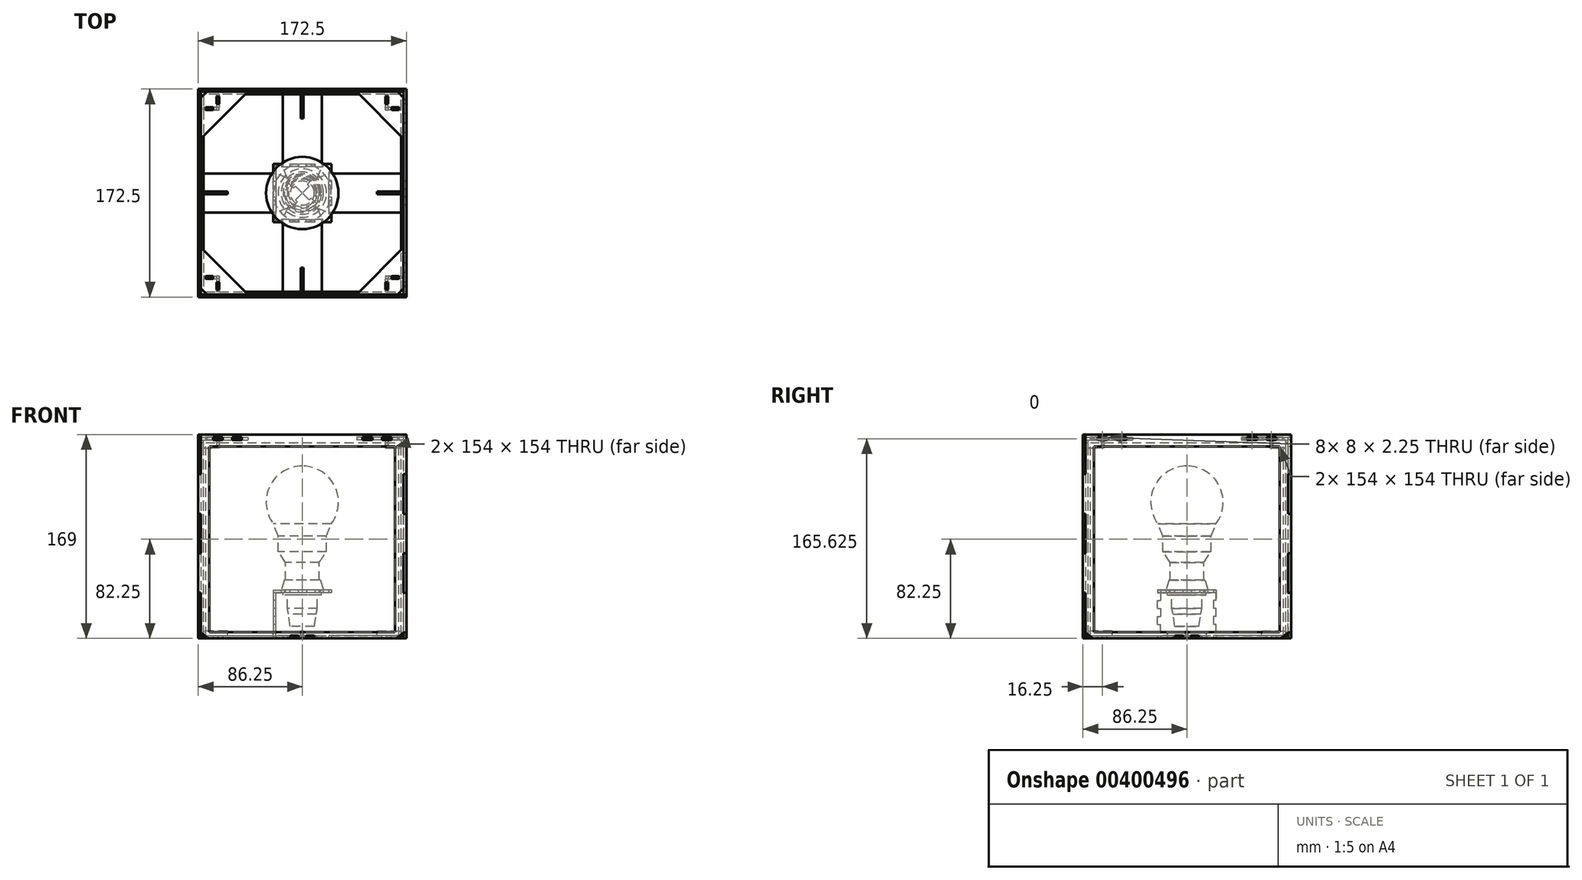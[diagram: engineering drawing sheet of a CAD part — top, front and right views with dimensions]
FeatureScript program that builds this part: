
annotation { "Feature Type Name" : "Feature", "Feature Type Description" : "" }
export const myFeature = defineFeature(function(context is Context, id is Id, definition is map)
    precondition{}
    {
        {
            assignVariable(context, id + "F0", {"name" : "ep", "anyValue" : 2.25});
        }
        {
            var Q0;
            Q0=qCreatedBy(makeId("Front.planeOp"),FACE);
            var sketch = newSketch(context, id + "F1", { "sketchPlane" : qUnion([Q0])});
            skLineSegment(sketch, "E0", {"start": v(0, 10) * mm, "end": v(10, 10) * mm});
            skLineSegment(sketch, "E1", {"start": v(10, 10) * mm, "end": v(11.5, 20) * mm});
            skLineSegment(sketch, "E2", {"start": v(11.5, 20) * mm, "end": v(12.5, 25) * mm});
            skLineSegment(sketch, "E3", {"start": v(12.5, 25) * mm, "end": v(12.5, 36) * mm});
            skLineSegment(sketch, "E4", {"start": v(12.5, 36) * mm, "end": v(16, 36) * mm});
            skLineSegment(sketch, "E5", {"start": v(16, 36) * mm, "end": v(16, 38) * mm});
            skLineSegment(sketch, "E6", {"start": v(16, 38) * mm, "end": v(14, 38) * mm});
            skLineSegment(sketch, "E7", {"start": v(14, 38) * mm, "end": v(14, 40.25) * mm});
            skLineSegment(sketch, "E8", {"start": v(14, 40.25) * mm, "end": v(17.5, 40.25) * mm});
            skLineSegment(sketch, "E9", {"start": v(17.5, 40.25) * mm, "end": v(15, 48.25) * mm});
            skLineSegment(sketch, "E10", {"start": v(15, 48.25) * mm, "end": v(14, 48.25) * mm});
            skLineSegment(sketch, "E11", {"start": v(14, 48.25) * mm, "end": v(14, 63) * mm});
            skLineSegment(sketch, "E12", {"start": v(14, 63) * mm, "end": v(20, 72) * mm});
            skLineSegment(sketch, "E13", {"start": v(20, 72) * mm, "end": v(20, 85) * mm});
            skLineSegment(sketch, "E14", {"start": v(20, 85) * mm, "end": v(24, 95) * mm});
            skLineSegment(sketch, "E15", {"start": v(0, 10) * mm, "end": v(0, 113) * mm, "construction": true});
            skArc(sketch, "E16", {"start": v(24, 95) * mm, "mid": v(26.83, 126.42) * mm, "end": v(0, 143) * mm});
            skLineSegment(sketch, "E17", {"start": v(0, 143) * mm, "end": v(0, 10) * mm});
            skSolve(sketch);
        }
        {
            var Q0;
            Q0=qSketchRegion(id+"F1",true);
            var Q1;
            Q1=sQuery(id+"F1.wireOp",EDGE,"E17");
            revolve(context, id + "F2", {"entities" : qUnion([Q0]), "axis" : qUnion([Q1]), "revolveType" : RevolveType.FULL});
        }
        {
            var Q0;
            Q0=makeQuery(id+"F2.opRevolve","SWEPT_FACE",FACE,{"disambiguationData":[OSD([sQuery(id+"F1.wireOp",EDGE,"E6")])]});
            var sketch = newSketch(context, id + "F3", { "sketchPlane" : qUnion([Q0])});
            skCircle(sketch, "E18.0", {"center": v(0, 0) * mm, "radius": 15 * mm});
            skLineSegment(sketch, "E19.top", {"start": v(-17.32, 22) * mm, "end": v(-10.4, 22) * mm});
            skLineSegment(sketch, "E19.left", {"start": v(-17.32, 24.25) * mm, "end": v(-17.32, 22) * mm});
            skLineSegment(sketch, "E19.right", {"start": v(-10.4, 24.25) * mm, "end": v(-10.4, 22) * mm});
            skLineSegment(sketch, "E20.1.0.0", {"start": v(3.46, 24.25) * mm, "end": v(3.46, 22) * mm});
            skLineSegment(sketch, "E20.1.0.1", {"start": v(-3.46, 22) * mm, "end": v(3.46, 22) * mm});
            skLineSegment(sketch, "E20.1.0.3", {"start": v(-3.46, 24.25) * mm, "end": v(-3.46, 22) * mm});
            skLineSegment(sketch, "E20.2.0.0", {"start": v(17.32, 24.25) * mm, "end": v(17.32, 22) * mm});
            skLineSegment(sketch, "E20.2.0.1", {"start": v(10.4, 22) * mm, "end": v(17.32, 22) * mm});
            skLineSegment(sketch, "E20.2.0.3", {"start": v(10.4, 24.25) * mm, "end": v(10.4, 22) * mm});
            skLineSegment(sketch, "E21", {"start": v(-24.25, 24.25) * mm, "end": v(-17.32, 24.25) * mm});
            skLineSegment(sketch, "E22", {"start": v(-10.4, 24.25) * mm, "end": v(-3.46, 24.25) * mm});
            skLineSegment(sketch, "E23", {"start": v(3.46, 24.25) * mm, "end": v(10.4, 24.25) * mm});
            skLineSegment(sketch, "E24", {"start": v(17.32, 24.25) * mm, "end": v(24.25, 24.25) * mm});
            skLineSegment(sketch, "E25.1.0", {"start": v(-24.25, -3.46) * mm, "end": v(-22, -3.46) * mm});
            skLineSegment(sketch, "E25.1.1", {"start": v(-22, -3.46) * mm, "end": v(-22, 3.46) * mm});
            skLineSegment(sketch, "E25.1.2", {"start": v(-24.25, 17.32) * mm, "end": v(-22, 17.32) * mm});
            skLineSegment(sketch, "E25.1.3", {"start": v(-24.25, 3.46) * mm, "end": v(-24.25, 10.4) * mm});
            skLineSegment(sketch, "E25.1.4", {"start": v(-24.25, 3.46) * mm, "end": v(-22, 3.46) * mm});
            skLineSegment(sketch, "E25.1.5", {"start": v(-24.25, -10.4) * mm, "end": v(-24.25, -3.46) * mm});
            skLineSegment(sketch, "E25.1.6", {"start": v(-24.25, -10.4) * mm, "end": v(-22, -10.4) * mm});
            skLineSegment(sketch, "E25.1.7", {"start": v(-24.25, -24.25) * mm, "end": v(-24.25, -17.32) * mm});
            skLineSegment(sketch, "E25.1.8", {"start": v(-24.25, 10.4) * mm, "end": v(-22, 10.4) * mm});
            skLineSegment(sketch, "E25.1.9", {"start": v(-24.25, -17.32) * mm, "end": v(-22, -17.32) * mm});
            skLineSegment(sketch, "E25.1.10", {"start": v(-22, 10.4) * mm, "end": v(-22, 17.32) * mm});
            skLineSegment(sketch, "E25.1.11", {"start": v(-24.25, 17.32) * mm, "end": v(-24.25, 24.25) * mm});
            skLineSegment(sketch, "E25.1.12", {"start": v(-22, -17.32) * mm, "end": v(-22, -10.4) * mm});
            skLineSegment(sketch, "E25.2.0", {"start": v(3.46, -24.25) * mm, "end": v(3.46, -22) * mm});
            skLineSegment(sketch, "E25.2.1", {"start": v(3.46, -22) * mm, "end": v(-3.46, -22) * mm});
            skLineSegment(sketch, "E25.2.2", {"start": v(-17.32, -24.25) * mm, "end": v(-17.32, -22) * mm});
            skLineSegment(sketch, "E25.2.3", {"start": v(-3.46, -24.25) * mm, "end": v(-10.4, -24.25) * mm});
            skLineSegment(sketch, "E25.2.4", {"start": v(-3.46, -24.25) * mm, "end": v(-3.46, -22) * mm});
            skLineSegment(sketch, "E25.2.5", {"start": v(10.4, -24.25) * mm, "end": v(3.46, -24.25) * mm});
            skLineSegment(sketch, "E25.2.6", {"start": v(10.4, -24.25) * mm, "end": v(10.4, -22) * mm});
            skLineSegment(sketch, "E25.2.7", {"start": v(24.25, -24.25) * mm, "end": v(17.32, -24.25) * mm});
            skLineSegment(sketch, "E25.2.8", {"start": v(-10.4, -24.25) * mm, "end": v(-10.4, -22) * mm});
            skLineSegment(sketch, "E25.2.9", {"start": v(17.32, -24.25) * mm, "end": v(17.32, -22) * mm});
            skLineSegment(sketch, "E25.2.10", {"start": v(-10.4, -22) * mm, "end": v(-17.32, -22) * mm});
            skLineSegment(sketch, "E25.2.11", {"start": v(-17.32, -24.25) * mm, "end": v(-24.25, -24.25) * mm});
            skLineSegment(sketch, "E25.2.12", {"start": v(17.32, -22) * mm, "end": v(10.4, -22) * mm});
            skLineSegment(sketch, "E25.3.0", {"start": v(24.25, 3.46) * mm, "end": v(22, 3.46) * mm});
            skLineSegment(sketch, "E25.3.1", {"start": v(22, 3.46) * mm, "end": v(22, -3.46) * mm});
            skLineSegment(sketch, "E25.3.2", {"start": v(24.25, -17.32) * mm, "end": v(22, -17.32) * mm});
            skLineSegment(sketch, "E25.3.3", {"start": v(24.25, -3.46) * mm, "end": v(24.25, -10.4) * mm});
            skLineSegment(sketch, "E25.3.4", {"start": v(24.25, -3.46) * mm, "end": v(22, -3.46) * mm});
            skLineSegment(sketch, "E25.3.5", {"start": v(24.25, 10.4) * mm, "end": v(24.25, 3.46) * mm});
            skLineSegment(sketch, "E25.3.6", {"start": v(24.25, 10.4) * mm, "end": v(22, 10.4) * mm});
            skLineSegment(sketch, "E25.3.7", {"start": v(24.25, 24.25) * mm, "end": v(24.25, 17.32) * mm});
            skLineSegment(sketch, "E25.3.8", {"start": v(24.25, -10.4) * mm, "end": v(22, -10.4) * mm});
            skLineSegment(sketch, "E25.3.9", {"start": v(24.25, 17.32) * mm, "end": v(22, 17.32) * mm});
            skLineSegment(sketch, "E25.3.10", {"start": v(22, -10.4) * mm, "end": v(22, -17.32) * mm});
            skLineSegment(sketch, "E25.3.11", {"start": v(24.25, -17.32) * mm, "end": v(24.25, -24.25) * mm});
            skLineSegment(sketch, "E25.3.12", {"start": v(22, 17.32) * mm, "end": v(22, 10.4) * mm});
            skSolve(sketch);
        }
        {
            var Q0;
            Q0=makeQuery(id+"F3.imprint","IMPRINT",FACE,{"disambiguationData":[TD([[makeQuery(id+"F3.imprint","IMPRINT",EDGE,{"derivedFrom":sQuery(id+"F3.wireOp",EDGE,"E19.top")}),-1.0]])]});
            var Q1;
            Q1=makeQuery(id+"F3.imprint","IMPRINT",FACE,{"disambiguationData":[TD([[makeQuery(id+"F3.imprint","IMPRINT",EDGE,{"derivedFrom":sQuery(id+"F3.wireOp",EDGE,"E18.0")}),-1.0]])]});
            extrude(context, id + "F4", {"entities" : qUnion([Q0, Q1]), "depth" : (getVariable(context, 'ep')) * mm});
        }
        {
            var Q0;
            Q0=makeQuery(id+"F4.opExtrude","CAP_FACE",FACE,{"disambiguationData":[OSD([sQuery(id+"F3.wireOp",EDGE,"E18.0"),sQuery(id+"F3.wireOp",EDGE,"E19.top"),sQuery(id+"F3.wireOp",EDGE,"E19.left"),sQuery(id+"F3.wireOp",EDGE,"E19.right"),sQuery(id+"F3.wireOp",EDGE,"E20.1.0.0"),sQuery(id+"F3.wireOp",EDGE,"E20.1.0.1"),sQuery(id+"F3.wireOp",EDGE,"E20.1.0.3"),sQuery(id+"F3.wireOp",EDGE,"E20.2.0.0"),sQuery(id+"F3.wireOp",EDGE,"E20.2.0.1"),sQuery(id+"F3.wireOp",EDGE,"E20.2.0.3"),sQuery(id+"F3.wireOp",EDGE,"E21"),sQuery(id+"F3.wireOp",EDGE,"E22"),sQuery(id+"F3.wireOp",EDGE,"E23"),sQuery(id+"F3.wireOp",EDGE,"E24"),sQuery(id+"F3.wireOp",EDGE,"E25.1.0"),sQuery(id+"F3.wireOp",EDGE,"E25.1.1"),sQuery(id+"F3.wireOp",EDGE,"E25.1.2"),sQuery(id+"F3.wireOp",EDGE,"E25.1.3"),sQuery(id+"F3.wireOp",EDGE,"E25.1.4"),sQuery(id+"F3.wireOp",EDGE,"E25.1.5"),sQuery(id+"F3.wireOp",EDGE,"E25.1.6"),sQuery(id+"F3.wireOp",EDGE,"E25.1.7"),sQuery(id+"F3.wireOp",EDGE,"E25.1.8"),sQuery(id+"F3.wireOp",EDGE,"E25.1.9"),sQuery(id+"F3.wireOp",EDGE,"E25.1.10"),sQuery(id+"F3.wireOp",EDGE,"E25.1.11"),sQuery(id+"F3.wireOp",EDGE,"E25.1.12"),sQuery(id+"F3.wireOp",EDGE,"E25.2.0"),sQuery(id+"F3.wireOp",EDGE,"E25.2.1"),sQuery(id+"F3.wireOp",EDGE,"E25.2.2"),sQuery(id+"F3.wireOp",EDGE,"E25.2.3"),sQuery(id+"F3.wireOp",EDGE,"E25.2.4"),sQuery(id+"F3.wireOp",EDGE,"E25.2.5"),sQuery(id+"F3.wireOp",EDGE,"E25.2.6"),sQuery(id+"F3.wireOp",EDGE,"E25.2.7"),sQuery(id+"F3.wireOp",EDGE,"E25.2.8"),sQuery(id+"F3.wireOp",EDGE,"E25.2.9"),sQuery(id+"F3.wireOp",EDGE,"E25.2.10"),sQuery(id+"F3.wireOp",EDGE,"E25.2.11"),sQuery(id+"F3.wireOp",EDGE,"E25.2.12"),sQuery(id+"F3.wireOp",EDGE,"E25.3.0"),sQuery(id+"F3.wireOp",EDGE,"E25.3.1"),sQuery(id+"F3.wireOp",EDGE,"E25.3.2"),sQuery(id+"F3.wireOp",EDGE,"E25.3.3"),sQuery(id+"F3.wireOp",EDGE,"E25.3.4"),sQuery(id+"F3.wireOp",EDGE,"E25.3.5"),sQuery(id+"F3.wireOp",EDGE,"E25.3.6"),sQuery(id+"F3.wireOp",EDGE,"E25.3.7"),sQuery(id+"F3.wireOp",EDGE,"E25.3.8"),sQuery(id+"F3.wireOp",EDGE,"E25.3.9"),sQuery(id+"F3.wireOp",EDGE,"E25.3.10"),sQuery(id+"F3.wireOp",EDGE,"E25.3.11"),sQuery(id+"F3.wireOp",EDGE,"E25.3.12")])],"isStart":true});
            var sketch = newSketch(context, id + "F5", { "sketchPlane" : qUnion([Q0])});
            skLineSegment(sketch, "E26.left", {"start": v(-24.25, 24.25) * mm, "end": v(-24.25, -24.25) * mm});
            skLineSegment(sketch, "E26.right", {"start": v(24.25, 24.25) * mm, "end": v(24.25, -24.25) * mm});
            skLineSegment(sketch, "E27", {"start": v(22, 24.25) * mm, "end": v(22, -24.25) * mm});
            skLineSegment(sketch, "E28", {"start": v(22, -24.25) * mm, "end": v(24.25, -24.25) * mm});
            skLineSegment(sketch, "E29", {"start": v(22, 24.25) * mm, "end": v(24.25, 24.25) * mm});
            skLineSegment(sketch, "E30", {"start": v(-22, 24.25) * mm, "end": v(-22, -24.25) * mm});
            skLineSegment(sketch, "E31", {"start": v(-22, -24.25) * mm, "end": v(-24.25, -24.25) * mm});
            skLineSegment(sketch, "E32", {"start": v(-24.25, 24.25) * mm, "end": v(-22, 24.25) * mm});
            skSolve(sketch);
        }
        {
            var Q0;
            {var subQ0=sQuery(id+"F5.wireOp",EDGE,"E32");Q0=makeQuery(id+"F5.imprint","IMPRINT",FACE,{"disambiguationData":[TD([[makeQuery(id+"F5.imprint","IMPRINT",EDGE,{"derivedFrom":subQ0}),1.0]])]});}
            var Q1;
            {var subQ1=makeQuery(id+"F4.opExtrude","CAP_EDGE",EDGE,{"disambiguationData":[OSD([sQuery(id+"F3.wireOp",EDGE,"E25.1.6")])],"isStart":true});Q1=makeQuery(id+"F5.imprint","IMPRINT",FACE,{"disambiguationData":[TD([[makeQuery(id+"F5.imprint","IMPRINT",EDGE,{"derivedFrom":subQ1}),1.0]])]});}
            var Q2;
            {var subQ1=makeQuery(id+"F4.opExtrude","CAP_EDGE",EDGE,{"disambiguationData":[OSD([sQuery(id+"F3.wireOp",EDGE,"E25.1.0")])],"isStart":true});Q2=makeQuery(id+"F5.imprint","IMPRINT",FACE,{"disambiguationData":[TD([[makeQuery(id+"F5.imprint","IMPRINT",EDGE,{"derivedFrom":subQ1}),1.0]])]});}
            var Q3;
            {var subQ1=makeQuery(id+"F4.opExtrude","CAP_EDGE",EDGE,{"disambiguationData":[OSD([sQuery(id+"F3.wireOp",EDGE,"E25.1.0")])],"isStart":true});Q3=makeQuery(id+"F5.imprint","IMPRINT",FACE,{"disambiguationData":[TD([[makeQuery(id+"F5.imprint","IMPRINT",EDGE,{"derivedFrom":subQ1}),-1.0]])]});}
            var Q4;
            {var subQ1=makeQuery(id+"F4.opExtrude","CAP_EDGE",EDGE,{"disambiguationData":[OSD([sQuery(id+"F3.wireOp",EDGE,"E25.1.4")])],"isStart":true});Q4=makeQuery(id+"F5.imprint","IMPRINT",FACE,{"disambiguationData":[TD([[makeQuery(id+"F5.imprint","IMPRINT",EDGE,{"derivedFrom":subQ1}),-1.0]])]});}
            var Q5;
            {var subQ1=makeQuery(id+"F4.opExtrude","CAP_EDGE",EDGE,{"disambiguationData":[OSD([sQuery(id+"F3.wireOp",EDGE,"E25.1.2")])],"isStart":true});Q5=makeQuery(id+"F5.imprint","IMPRINT",FACE,{"disambiguationData":[TD([[makeQuery(id+"F5.imprint","IMPRINT",EDGE,{"derivedFrom":subQ1}),1.0]])]});}
            var Q6;
            {var subQ0=sQuery(id+"F5.wireOp",EDGE,"E31");Q6=makeQuery(id+"F5.imprint","IMPRINT",FACE,{"disambiguationData":[TD([[makeQuery(id+"F5.imprint","IMPRINT",EDGE,{"derivedFrom":subQ0}),1.0]])]});}
            var Q7;
            Q7=qCreatedBy(makeId("Top.planeOp"),FACE);
            extrude(context, id + "F6", {"entities" : qUnion([Q0, Q1, Q2, Q3, Q4, Q5, Q6]), "endBound" : BoundingType.UP_TO_SURFACE, "endBoundEntityFace" : qUnion([Q7]), "depth" : 25 * mm});
        }
        {
            var Q0;
            {var subQ1=makeQuery(id+"F4.opExtrude","CAP_EDGE",EDGE,{"disambiguationData":[OSD([sQuery(id+"F3.wireOp",EDGE,"E25.1.2")])],"isStart":true});Q0=makeQuery(id+"F5.imprint","IMPRINT",FACE,{"disambiguationData":[TD([[makeQuery(id+"F5.imprint","IMPRINT",EDGE,{"derivedFrom":subQ1}),1.0]])]});}
            var Q1;
            {var subQ1=makeQuery(id+"F4.opExtrude","CAP_EDGE",EDGE,{"disambiguationData":[OSD([sQuery(id+"F3.wireOp",EDGE,"E25.1.0")])],"isStart":true});Q1=makeQuery(id+"F5.imprint","IMPRINT",FACE,{"disambiguationData":[TD([[makeQuery(id+"F5.imprint","IMPRINT",EDGE,{"derivedFrom":subQ1}),-1.0]])]});}
            var Q2;
            {var subQ1=makeQuery(id+"F4.opExtrude","CAP_EDGE",EDGE,{"disambiguationData":[OSD([sQuery(id+"F3.wireOp",EDGE,"E25.1.6")])],"isStart":true});Q2=makeQuery(id+"F5.imprint","IMPRINT",FACE,{"disambiguationData":[TD([[makeQuery(id+"F5.imprint","IMPRINT",EDGE,{"derivedFrom":subQ1}),1.0]])]});}
            var Q3;
            Q3=makeQuery(id+"F4.opExtrude","CAP_FACE",FACE,{"disambiguationData":[OSD([sQuery(id+"F3.wireOp",EDGE,"E18.0"),sQuery(id+"F3.wireOp",EDGE,"E19.top"),sQuery(id+"F3.wireOp",EDGE,"E19.left"),sQuery(id+"F3.wireOp",EDGE,"E19.right"),sQuery(id+"F3.wireOp",EDGE,"E20.1.0.0"),sQuery(id+"F3.wireOp",EDGE,"E20.1.0.1"),sQuery(id+"F3.wireOp",EDGE,"E20.1.0.3"),sQuery(id+"F3.wireOp",EDGE,"E20.2.0.0"),sQuery(id+"F3.wireOp",EDGE,"E20.2.0.1"),sQuery(id+"F3.wireOp",EDGE,"E20.2.0.3"),sQuery(id+"F3.wireOp",EDGE,"E21"),sQuery(id+"F3.wireOp",EDGE,"E22"),sQuery(id+"F3.wireOp",EDGE,"E23"),sQuery(id+"F3.wireOp",EDGE,"E24"),sQuery(id+"F3.wireOp",EDGE,"E25.1.0"),sQuery(id+"F3.wireOp",EDGE,"E25.1.1"),sQuery(id+"F3.wireOp",EDGE,"E25.1.2"),sQuery(id+"F3.wireOp",EDGE,"E25.1.3"),sQuery(id+"F3.wireOp",EDGE,"E25.1.4"),sQuery(id+"F3.wireOp",EDGE,"E25.1.5"),sQuery(id+"F3.wireOp",EDGE,"E25.1.6"),sQuery(id+"F3.wireOp",EDGE,"E25.1.7"),sQuery(id+"F3.wireOp",EDGE,"E25.1.8"),sQuery(id+"F3.wireOp",EDGE,"E25.1.9"),sQuery(id+"F3.wireOp",EDGE,"E25.1.10"),sQuery(id+"F3.wireOp",EDGE,"E25.1.11"),sQuery(id+"F3.wireOp",EDGE,"E25.1.12"),sQuery(id+"F3.wireOp",EDGE,"E25.2.0"),sQuery(id+"F3.wireOp",EDGE,"E25.2.1"),sQuery(id+"F3.wireOp",EDGE,"E25.2.2"),sQuery(id+"F3.wireOp",EDGE,"E25.2.3"),sQuery(id+"F3.wireOp",EDGE,"E25.2.4"),sQuery(id+"F3.wireOp",EDGE,"E25.2.5"),sQuery(id+"F3.wireOp",EDGE,"E25.2.6"),sQuery(id+"F3.wireOp",EDGE,"E25.2.7"),sQuery(id+"F3.wireOp",EDGE,"E25.2.8"),sQuery(id+"F3.wireOp",EDGE,"E25.2.9"),sQuery(id+"F3.wireOp",EDGE,"E25.2.10"),sQuery(id+"F3.wireOp",EDGE,"E25.2.11"),sQuery(id+"F3.wireOp",EDGE,"E25.2.12"),sQuery(id+"F3.wireOp",EDGE,"E25.3.0"),sQuery(id+"F3.wireOp",EDGE,"E25.3.1"),sQuery(id+"F3.wireOp",EDGE,"E25.3.2"),sQuery(id+"F3.wireOp",EDGE,"E25.3.3"),sQuery(id+"F3.wireOp",EDGE,"E25.3.4"),sQuery(id+"F3.wireOp",EDGE,"E25.3.5"),sQuery(id+"F3.wireOp",EDGE,"E25.3.6"),sQuery(id+"F3.wireOp",EDGE,"E25.3.7"),sQuery(id+"F3.wireOp",EDGE,"E25.3.8"),sQuery(id+"F3.wireOp",EDGE,"E25.3.9"),sQuery(id+"F3.wireOp",EDGE,"E25.3.10"),sQuery(id+"F3.wireOp",EDGE,"E25.3.11"),sQuery(id+"F3.wireOp",EDGE,"E25.3.12")])],"isStart":false});
            extrude(context, id + "F7", {"entities" : qUnion([Q0, Q1, Q2]), "operationType" : NewBodyOperationType.ADD, "endBound" : BoundingType.UP_TO_SURFACE, "oppositeDirection" : true, "endBoundEntityFace" : qUnion([Q3]), "depth" : 25 * mm});
        }
        {
            var Q0;
            {var subQ0=sQuery(id+"F5.wireOp",EDGE,"E26.left");Q0=makeQuery(id+"F7.boolean.opBoolean","MERGE",FACE,{"derivedFrom":[makeQuery(id+"F6.opExtrude","SWEPT_FACE",FACE,{"disambiguationData":[OSD([subQ0])]}),makeQuery(id+"F7.opExtrude","SWEPT_FACE",FACE,{"disambiguationData":[OSD([subQ0]),TDD([makeQuery(id+"F5.imprint","IMPRINT",EDGE,{"disambiguationData":[TD([[makeQuery(id+"F5.imprint","INTERSECT",VERTEX,{"derivedFrom":[makeQuery(id+"F4.opExtrude","CAP_EDGE",EDGE,{"disambiguationData":[OSD([sQuery(id+"F3.wireOp",EDGE,"E25.1.6")])],"isStart":true}),subQ0]}),1.0]])],"derivedFrom":subQ0})])]}),makeQuery(id+"F7.opExtrude","SWEPT_FACE",FACE,{"disambiguationData":[OSD([subQ0]),TDD([makeQuery(id+"F5.imprint","IMPRINT",EDGE,{"disambiguationData":[TD([[makeQuery(id+"F5.imprint","INTERSECT",VERTEX,{"derivedFrom":[makeQuery(id+"F4.opExtrude","CAP_EDGE",EDGE,{"disambiguationData":[OSD([sQuery(id+"F3.wireOp",EDGE,"E25.1.0")])],"isStart":true}),subQ0]}),-1.0]])],"derivedFrom":subQ0})])]}),makeQuery(id+"F7.opExtrude","SWEPT_FACE",FACE,{"disambiguationData":[OSD([subQ0]),TDD([makeQuery(id+"F5.imprint","IMPRINT",EDGE,{"disambiguationData":[TD([[makeQuery(id+"F5.imprint","INTERSECT",VERTEX,{"derivedFrom":[makeQuery(id+"F4.opExtrude","CAP_EDGE",EDGE,{"disambiguationData":[OSD([sQuery(id+"F3.wireOp",EDGE,"E25.1.2")])],"isStart":true}),subQ0]}),1.0]])],"derivedFrom":subQ0})])]})]});}
            var sketch = newSketch(context, id + "F8", { "sketchPlane" : qUnion([Q0])});
            skLineSegment(sketch, "E33.bottom", {"start": v(-24.25, 0) * mm, "end": v(-9.75, 0) * mm});
            skLineSegment(sketch, "E33.top", {"start": v(-24.25, 5) * mm, "end": v(-16.25, 5) * mm});
            skLineSegment(sketch, "E33.left", {"start": v(-24.25, 0) * mm, "end": v(-24.25, 5) * mm});
            skLineSegment(sketch, "E33.right", {"start": v(-16.25, 2.25) * mm, "end": v(-16.25, 5) * mm});
            skLineSegment(sketch, "E34.bottom", {"start": v(24.25, 0) * mm, "end": v(9.75, 0) * mm});
            skLineSegment(sketch, "E34.top", {"start": v(22, 5) * mm, "end": v(16.25, 5) * mm});
            skLineSegment(sketch, "E34.left", {"start": v(24.25, 0) * mm, "end": v(24.25, 5) * mm});
            skLineSegment(sketch, "E34.right", {"start": v(16.25, 2.25) * mm, "end": v(16.25, 5) * mm});
            skLineSegment(sketch, "E35.bottom", {"start": v(-24.25, 31.4) * mm, "end": v(-22, 31.4) * mm});
            skLineSegment(sketch, "E35.top", {"start": v(-24.25, 24.8) * mm, "end": v(-22, 24.8) * mm});
            skLineSegment(sketch, "E35.left", {"start": v(-24.25, 31.4) * mm, "end": v(-24.25, 24.8) * mm});
            skLineSegment(sketch, "E35.right", {"start": v(-22, 31.4) * mm, "end": v(-22, 24.8) * mm});
            skLineSegment(sketch, "E36.bottom", {"start": v(-24.25, 18.2) * mm, "end": v(-22, 18.2) * mm});
            skLineSegment(sketch, "E36.top", {"start": v(-24.25, 11.6) * mm, "end": v(-22, 11.6) * mm});
            skLineSegment(sketch, "E36.left", {"start": v(-24.25, 18.2) * mm, "end": v(-24.25, 11.6) * mm});
            skLineSegment(sketch, "E36.right", {"start": v(-22, 18.2) * mm, "end": v(-22, 11.6) * mm});
            skLineSegment(sketch, "E37", {"start": v(-24.25, 38) * mm, "end": v(-24.25, 31.4) * mm, "construction": true});
            skLineSegment(sketch, "E38", {"start": v(-24.25, 24.8) * mm, "end": v(-24.25, 18.2) * mm, "construction": true});
            skLineSegment(sketch, "E39", {"start": v(-24.25, 11.6) * mm, "end": v(-24.25, 5) * mm, "construction": true});
            skLineSegment(sketch, "E40.bottom", {"start": v(24.25, 38) * mm, "end": v(22, 38) * mm});
            skLineSegment(sketch, "E40.top", {"start": v(24.25, 31.4) * mm, "end": v(22, 31.4) * mm});
            skLineSegment(sketch, "E40.left", {"start": v(24.25, 38) * mm, "end": v(24.25, 31.4) * mm});
            skLineSegment(sketch, "E40.right", {"start": v(22, 38) * mm, "end": v(22, 31.4) * mm});
            skLineSegment(sketch, "E41.bottom", {"start": v(24.25, 24.8) * mm, "end": v(22, 24.8) * mm});
            skLineSegment(sketch, "E41.top", {"start": v(24.25, 18.2) * mm, "end": v(22, 18.2) * mm});
            skLineSegment(sketch, "E41.left", {"start": v(24.25, 24.8) * mm, "end": v(24.25, 18.2) * mm});
            skLineSegment(sketch, "E41.right", {"start": v(22, 24.8) * mm, "end": v(22, 18.2) * mm});
            skLineSegment(sketch, "E42.top", {"start": v(24.25, 11.6) * mm, "end": v(22, 11.6) * mm});
            skLineSegment(sketch, "E42.left", {"start": v(24.25, 5) * mm, "end": v(24.25, 11.6) * mm});
            skLineSegment(sketch, "E42.right", {"start": v(22, 5) * mm, "end": v(22, 11.6) * mm});
            skLineSegment(sketch, "E43", {"start": v(24.25, 31.4) * mm, "end": v(24.25, 24.8) * mm, "construction": true});
            skLineSegment(sketch, "E44", {"start": v(24.25, 18.2) * mm, "end": v(24.25, 11.6) * mm, "construction": true});
            skLineSegment(sketch, "E45.bottom", {"start": v(-16.25, 2.25) * mm, "end": v(-9.75, 2.25) * mm});
            skLineSegment(sketch, "E45.right", {"start": v(-9.75, 2.25) * mm, "end": v(-9.75, 0) * mm});
            skLineSegment(sketch, "E46.bottom", {"start": v(-3.25, 0) * mm, "end": v(3.25, 0) * mm});
            skLineSegment(sketch, "E46.top", {"start": v(-3.25, 2.25) * mm, "end": v(3.25, 2.25) * mm});
            skLineSegment(sketch, "E46.left", {"start": v(-3.25, 0) * mm, "end": v(-3.25, 2.25) * mm});
            skLineSegment(sketch, "E46.right", {"start": v(3.25, 0) * mm, "end": v(3.25, 2.25) * mm});
            skLineSegment(sketch, "E47.top", {"start": v(9.75, 2.25) * mm, "end": v(16.25, 2.25) * mm});
            skLineSegment(sketch, "E47.left", {"start": v(9.75, 0) * mm, "end": v(9.75, 2.25) * mm});
            skLineSegment(sketch, "E48", {"start": v(-9.75, 0) * mm, "end": v(-3.25, 0) * mm, "construction": true});
            skLineSegment(sketch, "E49", {"start": v(3.25, 0) * mm, "end": v(9.75, 0) * mm, "construction": true});
            skSolve(sketch);
        }
        {
            var Q0;
            Q0=qSketchRegion(id+"F8",true);
            extrude(context, id + "F9", {"entities" : qUnion([Q0]), "operationType" : NewBodyOperationType.REMOVE, "endBound" : BoundingType.UP_TO_NEXT, "oppositeDirection" : true, "depth" : 25 * mm});
        }
        {
            var Q0;
            Q0=qCreatedBy(makeId("Right.planeOp"),FACE);
            cPlane(context, id + "F10", {"entities" : qUnion([Q0]), "cplaneType" : CPlaneType.OFFSET, "offset" : ((172.5) / 2 - 2 - getVariable(context, 'ep')) * mm, "oppositeDirection" : true, "width" : 150 * mm, "height" : 150 * mm});
        }
        {
            var Q0;
            Q0=qCreatedBy(id+"F10.planeOp",FACE);
            var sketch = newSketch(context, id + "F11", { "sketchPlane" : qUnion([Q0])});
            skLineSegment(sketch, "E50.bottom", {"start": v(80, 2.25) * mm, "end": v(-80, 2.25) * mm});
            skLineSegment(sketch, "E50.top", {"start": v(80, 162.25) * mm, "end": v(-80, 162.25) * mm});
            skLineSegment(sketch, "E50.left", {"start": v(80, 2.25) * mm, "end": v(80, 162.25) * mm});
            skLineSegment(sketch, "E50.right", {"start": v(-80, 2.25) * mm, "end": v(-80, 162.25) * mm});
            skPoint(sketch, "E50.middle", {"position": v(0, 82.25) * mm});
            skSolve(sketch);
        }
        {
            var Q0;
            Q0=makeQuery(id+"F11.imprint","IMPRINT",FACE,{"disambiguationData":[TD([[makeQuery(id+"F11.imprint","IMPRINT",EDGE,{"derivedFrom":sQuery(id+"F11.wireOp",EDGE,"E50.bottom")}),-1.0]])]});
            extrude(context, id + "F12", {"entities" : qUnion([Q0]), "oppositeDirection" : true, "depth" : 2 * mm});
        }
        {
            var Q0;
            Q0=makeQuery(id+"F12.opExtrude","CAP_FACE",FACE,{"disambiguationData":[OSD([sQuery(id+"F11.wireOp",EDGE,"E50.bottom"),sQuery(id+"F11.wireOp",EDGE,"E50.top"),sQuery(id+"F11.wireOp",EDGE,"E50.left"),sQuery(id+"F11.wireOp",EDGE,"E50.right")])],"isStart":false});
            var sketch = newSketch(context, id + "F13", { "sketchPlane" : qUnion([Q0])});
            skLineSegment(sketch, "E51.0", {"start": v(-77, 159.25) * mm, "end": v(-77, 5.25) * mm});
            skLineSegment(sketch, "E51.1", {"start": v(77, 159.25) * mm, "end": v(-77, 159.25) * mm});
            skLineSegment(sketch, "E51.2", {"start": v(77, 5.25) * mm, "end": v(77, 159.25) * mm});
            skLineSegment(sketch, "E51.3", {"start": v(-77, 5.25) * mm, "end": v(77, 5.25) * mm});
            skLineSegment(sketch, "E52.0", {"start": v(-86.25, 136.2) * mm, "end": v(-86.25, 103.4) * mm});
            skLineSegment(sketch, "E52.1", {"start": v(86.25, 169) * mm, "end": v(-84, 169) * mm});
            skLineSegment(sketch, "E52.2", {"start": v(86.25, 5) * mm, "end": v(86.25, 37.8) * mm});
            skLineSegment(sketch, "E52.3", {"start": v(-78, 0) * mm, "end": v(-9.75, 0) * mm});
            skLineSegment(sketch, "E53", {"start": v(-84, 5) * mm, "end": v(-78, 0) * mm});
            skLineSegment(sketch, "E54.top", {"start": v(-86.25, 136.2) * mm, "end": v(-84, 136.2) * mm});
            skLineSegment(sketch, "E54.right", {"start": v(-84, 169) * mm, "end": v(-84, 136.2) * mm});
            skLineSegment(sketch, "E55.bottom", {"start": v(-86.25, 103.4) * mm, "end": v(-84, 103.4) * mm});
            skLineSegment(sketch, "E55.top", {"start": v(-86.25, 70.6) * mm, "end": v(-84, 70.6) * mm});
            skLineSegment(sketch, "E55.right", {"start": v(-84, 103.4) * mm, "end": v(-84, 70.6) * mm});
            skLineSegment(sketch, "E56.bottom", {"start": v(-86.25, 37.8) * mm, "end": v(-84, 37.8) * mm});
            skLineSegment(sketch, "E56.right", {"start": v(-84, 37.8) * mm, "end": v(-84, 5) * mm});
            skLineSegment(sketch, "E57.trimOffspring", {"start": v(-86.25, 70.6) * mm, "end": v(-86.25, 37.8) * mm});
            skLineSegment(sketch, "E58.bottom", {"start": v(86.25, 136.2) * mm, "end": v(84, 136.2) * mm});
            skLineSegment(sketch, "E58.top", {"start": v(86.25, 103.4) * mm, "end": v(84, 103.4) * mm});
            skLineSegment(sketch, "E58.right", {"start": v(84, 136.2) * mm, "end": v(84, 103.4) * mm});
            skLineSegment(sketch, "E59.bottom", {"start": v(86.25, 70.6) * mm, "end": v(84, 70.6) * mm});
            skLineSegment(sketch, "E59.top", {"start": v(86.25, 37.8) * mm, "end": v(84, 37.8) * mm});
            skLineSegment(sketch, "E59.right", {"start": v(84, 70.6) * mm, "end": v(84, 37.8) * mm});
            skLineSegment(sketch, "E60.trimOffspring", {"start": v(86.25, 136.2) * mm, "end": v(86.25, 169) * mm});
            skLineSegment(sketch, "E61.trimOffspring", {"start": v(86.25, 70.6) * mm, "end": v(86.25, 103.4) * mm});
            skLineSegment(sketch, "E62", {"start": v(86.25, 5) * mm, "end": v(84, 5) * mm});
            skLineSegment(sketch, "E63", {"start": v(84, 5) * mm, "end": v(78, 0) * mm});
            skLineSegment(sketch, "E64.bottom", {"start": v(-74, 166.75) * mm, "end": v(-66, 166.75) * mm});
            skLineSegment(sketch, "E64.top", {"start": v(-74, 164.5) * mm, "end": v(-66, 164.5) * mm});
            skLineSegment(sketch, "E64.left", {"start": v(-74, 166.75) * mm, "end": v(-74, 164.5) * mm});
            skLineSegment(sketch, "E64.right", {"start": v(-66, 166.75) * mm, "end": v(-66, 164.5) * mm});
            skLineSegment(sketch, "E65.bottom", {"start": v(-58, 166.75) * mm, "end": v(-50, 166.75) * mm});
            skLineSegment(sketch, "E65.top", {"start": v(-58, 164.5) * mm, "end": v(-50, 164.5) * mm});
            skLineSegment(sketch, "E65.left", {"start": v(-58, 166.75) * mm, "end": v(-58, 164.5) * mm});
            skLineSegment(sketch, "E65.right", {"start": v(-50, 166.75) * mm, "end": v(-50, 164.5) * mm});
            skLineSegment(sketch, "E66", {"start": v(-66, 166.75) * mm, "end": v(-58, 166.75) * mm, "construction": true});
            skLineSegment(sketch, "E67.MirrorCS", {"start": v(74, 166.75) * mm, "end": v(74, 164.5) * mm});
            skLineSegment(sketch, "E68.MirrorCS", {"start": v(74, 166.75) * mm, "end": v(66, 166.75) * mm});
            skLineSegment(sketch, "E69.MirrorCS", {"start": v(66, 166.75) * mm, "end": v(66, 164.5) * mm});
            skLineSegment(sketch, "E70.MirrorCS", {"start": v(74, 164.5) * mm, "end": v(66, 164.5) * mm});
            skLineSegment(sketch, "E71.MirrorCS", {"start": v(58, 166.75) * mm, "end": v(58, 164.5) * mm});
            skLineSegment(sketch, "E72.MirrorCS", {"start": v(58, 166.75) * mm, "end": v(50, 166.75) * mm});
            skLineSegment(sketch, "E73.MirrorCS", {"start": v(58, 164.5) * mm, "end": v(50, 164.5) * mm});
            skLineSegment(sketch, "E74.MirrorCS", {"start": v(50, 166.75) * mm, "end": v(50, 164.5) * mm});
            skLineSegment(sketch, "E75.0", {"start": v(-9.75, 2.25) * mm, "end": v(-9.75, 0) * mm});
            skLineSegment(sketch, "E76.0", {"start": v(-3.25, 0) * mm, "end": v(-3.25, 2.25) * mm});
            skLineSegment(sketch, "E77.0", {"start": v(3.25, 0) * mm, "end": v(3.25, 2.25) * mm});
            skLineSegment(sketch, "E78.0", {"start": v(9.75, 0) * mm, "end": v(9.75, 2.25) * mm});
            skLineSegment(sketch, "E79", {"start": v(-9.75, 2.25) * mm, "end": v(-3.25, 2.25) * mm});
            skLineSegment(sketch, "E80", {"start": v(3.25, 2.25) * mm, "end": v(9.75, 2.25) * mm});
            skLineSegment(sketch, "E81.trimOffspring", {"start": v(-3.25, 0) * mm, "end": v(3.25, 0) * mm});
            skLineSegment(sketch, "E82.trimOffspring", {"start": v(9.75, 0) * mm, "end": v(78, 0) * mm});
            skSolve(sketch);
        }
        {
            var Q0;
            Q0=qSketchRegion(id+"F13",true);
            extrude(context, id + "F14", {"entities" : qUnion([Q0]), "depth" : (getVariable(context, 'ep')) * mm});
        }
        {
            var Q0;
            Q0=makeQuery(id+"F14.opExtrude","SWEPT_FACE",FACE,{"disambiguationData":[OSD([sQuery(id+"F13.wireOp",EDGE,"E64.top")])]});
            var sketch = newSketch(context, id + "F15", { "sketchPlane" : qUnion([Q0])});
            skLineSegment(sketch, "E83.0", {"start": v(-86.25, 74) * mm, "end": v(-84, 74) * mm});
            skLineSegment(sketch, "E84.0", {"start": v(-86.25, 74) * mm, "end": v(-86.25, 66) * mm});
            skLineSegment(sketch, "E85.0", {"start": v(-86.25, 66) * mm, "end": v(-84, 66) * mm});
            skLineSegment(sketch, "E86.0", {"start": v(-86.25, 58) * mm, "end": v(-84, 58) * mm});
            skLineSegment(sketch, "E87.0", {"start": v(-86.25, 58) * mm, "end": v(-86.25, 50) * mm});
            skLineSegment(sketch, "E88.0", {"start": v(-86.25, 50) * mm, "end": v(-84, 50) * mm});
            skLineSegment(sketch, "E89", {"start": v(-84, 66) * mm, "end": v(-84, 58) * mm});
            skLineSegment(sketch, "E90", {"start": v(-84, 74) * mm, "end": v(-84, 79) * mm});
            skLineSegment(sketch, "E91", {"start": v(-84, 50) * mm, "end": v(-84, 45) * mm});
            skLineSegment(sketch, "E92", {"start": v(0, 0) * mm, "end": v(-86.25, 86.25) * mm, "construction": true});
            skLineSegment(sketch, "E93.MirrorCS", {"start": v(-74, 84) * mm, "end": v(-79, 84) * mm});
            skLineSegment(sketch, "E94.MirrorCS", {"start": v(-74, 86.25) * mm, "end": v(-74, 84) * mm});
            skLineSegment(sketch, "E95.MirrorCS", {"start": v(-74, 86.25) * mm, "end": v(-66, 86.25) * mm});
            skLineSegment(sketch, "E96.MirrorCS", {"start": v(-66, 86.25) * mm, "end": v(-66, 84) * mm});
            skLineSegment(sketch, "E97.MirrorCS", {"start": v(-66, 84) * mm, "end": v(-58, 84) * mm});
            skLineSegment(sketch, "E98.MirrorCS", {"start": v(-58, 86.25) * mm, "end": v(-58, 84) * mm});
            skLineSegment(sketch, "E99.MirrorCS", {"start": v(-58, 86.25) * mm, "end": v(-50, 86.25) * mm});
            skLineSegment(sketch, "E100.MirrorCS", {"start": v(-50, 86.25) * mm, "end": v(-50, 84) * mm});
            skLineSegment(sketch, "E101.MirrorCS", {"start": v(-50, 84) * mm, "end": v(-45, 84) * mm});
            skLineSegment(sketch, "E102", {"start": v(-45, 84) * mm, "end": v(-84, 45) * mm});
            skLineSegment(sketch, "E103", {"start": v(-79, 84) * mm, "end": v(-84, 79) * mm});
            skLineSegment(sketch, "E104.bottom", {"start": v(-80, 71.13) * mm, "end": v(-74, 71.13) * mm});
            skLineSegment(sketch, "E104.top", {"start": v(-80, 68.88) * mm, "end": v(-74, 68.88) * mm});
            skLineSegment(sketch, "E104.left", {"start": v(-80, 71.13) * mm, "end": v(-80, 68.88) * mm});
            skLineSegment(sketch, "E104.right", {"start": v(-74, 71.13) * mm, "end": v(-74, 68.88) * mm});
            skLineSegment(sketch, "E105", {"start": v(-80, 70) * mm, "end": v(-84, 70) * mm, "construction": true});
            skLineSegment(sketch, "E106.MirrorCS", {"start": v(-71.13, 80) * mm, "end": v(-71.13, 74) * mm});
            skLineSegment(sketch, "E107.MirrorCS", {"start": v(-71.13, 74) * mm, "end": v(-68.88, 74) * mm});
            skLineSegment(sketch, "E108.MirrorCS", {"start": v(-68.88, 80) * mm, "end": v(-68.88, 74) * mm});
            skLineSegment(sketch, "E109.MirrorCS", {"start": v(-71.13, 80) * mm, "end": v(-68.88, 80) * mm});
            skSolve(sketch);
        }
        {
            var Q0;
            Q0=qSketchRegion(id+"F15",true);
            var Q1;
            Q1=makeQuery(id+"F14.opExtrude","SWEPT_FACE",FACE,{"disambiguationData":[OSD([sQuery(id+"F13.wireOp",EDGE,"E64.bottom")])]});
            extrude(context, id + "F16", {"entities" : qUnion([Q0]), "endBound" : BoundingType.UP_TO_SURFACE, "endBoundEntityFace" : qUnion([Q1]), "depth" : 25 * mm});
        }
        {
            var Q0;
            Q0=makeQuery(id+"F16.opExtrude","SWEPT_FACE",FACE,{"disambiguationData":[OSD([sQuery(id+"F15.wireOp",EDGE,"E104.bottom")])]});
            var sketch = newSketch(context, id + "F17", { "sketchPlane" : qUnion([Q0])});
            skLineSegment(sketch, "E110.0", {"start": v(-80, 166.75) * mm, "end": v(-80, 164.5) * mm});
            skLineSegment(sketch, "E111.0", {"start": v(-80, 166.75) * mm, "end": v(-74, 166.75) * mm});
            skLineSegment(sketch, "E112.0", {"start": v(-74, 166.75) * mm, "end": v(-74, 164.5) * mm});
            skLineSegment(sketch, "E113", {"start": v(-80, 164.5) * mm, "end": v(-82, 164.5) * mm});
            skLineSegment(sketch, "E114", {"start": v(-82, 164.5) * mm, "end": v(-82, 157.75) * mm});
            skLineSegment(sketch, "E115", {"start": v(-82, 157.75) * mm, "end": v(-68.88, 157.75) * mm});
            skLineSegment(sketch, "E116", {"start": v(-68.88, 157.75) * mm, "end": v(-68.88, 160) * mm});
            skLineSegment(sketch, "E117", {"start": v(-68.88, 160) * mm, "end": v(-71.13, 160) * mm});
            skLineSegment(sketch, "E118", {"start": v(-71.13, 160) * mm, "end": v(-71.13, 162.25) * mm});
            skLineSegment(sketch, "E119", {"start": v(-71.13, 162.25) * mm, "end": v(-68.88, 162.25) * mm});
            skLineSegment(sketch, "E120", {"start": v(-68.88, 162.25) * mm, "end": v(-68.88, 164.5) * mm});
            skLineSegment(sketch, "E121", {"start": v(-68.88, 164.5) * mm, "end": v(-74, 164.5) * mm});
            skSolve(sketch);
        }
        {
            var Q0;
            Q0=qSketchRegion(id+"F17",true);
            var Q1;
            Q1=makeQuery(id+"F16.opExtrude","SWEPT_FACE",FACE,{"disambiguationData":[OSD([sQuery(id+"F15.wireOp",EDGE,"E104.top")])]});
            extrude(context, id + "F18", {"entities" : qUnion([Q0]), "endBound" : BoundingType.UP_TO_SURFACE, "endBoundEntityFace" : qUnion([Q1]), "depth" : 25 * mm});
        }
        {
            var Q0;
            Q0=makeQuery(id+"F16.opExtrude","SWEPT_FACE",FACE,{"disambiguationData":[OSD([sQuery(id+"F15.wireOp",EDGE,"E106.MirrorCS")])]});
            var sketch = newSketch(context, id + "F19", { "sketchPlane" : qUnion([Q0])});
            skLineSegment(sketch, "E122.0", {"start": v(80, 166.75) * mm, "end": v(80, 164.5) * mm});
            skLineSegment(sketch, "E123.0", {"start": v(80, 166.75) * mm, "end": v(74, 166.75) * mm});
            skLineSegment(sketch, "E124.0", {"start": v(74, 166.75) * mm, "end": v(74, 164.5) * mm});
            skLineSegment(sketch, "E125.0", {"start": v(71.13, 162.25) * mm, "end": v(71.13, 164.5) * mm});
            skLineSegment(sketch, "E126.0", {"start": v(68.87, 162.25) * mm, "end": v(71.12, 162.25) * mm});
            skLineSegment(sketch, "E127.0", {"start": v(68.87, 162.25) * mm, "end": v(68.87, 160) * mm});
            skLineSegment(sketch, "E128.0", {"start": v(68.87, 160) * mm, "end": v(71.12, 160) * mm});
            skLineSegment(sketch, "E129.0", {"start": v(71.13, 157.75) * mm, "end": v(71.13, 160) * mm});
            skLineSegment(sketch, "E130", {"start": v(74, 164.5) * mm, "end": v(71.13, 164.5) * mm});
            skLineSegment(sketch, "E131", {"start": v(80, 164.5) * mm, "end": v(82, 164.5) * mm});
            skLineSegment(sketch, "E132", {"start": v(82, 164.5) * mm, "end": v(82, 157.75) * mm});
            skLineSegment(sketch, "E133", {"start": v(82, 157.75) * mm, "end": v(71.13, 157.75) * mm});
            skSolve(sketch);
        }
        {
            var Q0;
            Q0=qSketchRegion(id+"F19",true);
            var Q1;
            Q1=makeQuery(id+"F16.opExtrude","SWEPT_FACE",FACE,{"disambiguationData":[OSD([sQuery(id+"F15.wireOp",EDGE,"E108.MirrorCS")])]});
            extrude(context, id + "F20", {"entities" : qUnion([Q0]), "endBound" : BoundingType.UP_TO_SURFACE, "endBoundEntityFace" : qUnion([Q1]), "depth" : 25 * mm});
        }
        {
            var Q0;
            Q0=qCreatedBy(makeId("Top.planeOp"),FACE);
            var sketch = newSketch(context, id + "F21", { "sketchPlane" : qUnion([Q0])});
            skLineSegment(sketch, "E134.0.0", {"start": v(-24.25, 9.75) * mm, "end": v(-22, 9.75) * mm});
            skLineSegment(sketch, "E134.0.1", {"start": v(-22, 9.75) * mm, "end": v(-22, 3.25) * mm});
            skLineSegment(sketch, "E134.0.2", {"start": v(-22, 3.25) * mm, "end": v(-24.25, 3.25) * mm});
            skLineSegment(sketch, "E134.0.3", {"start": v(-24.25, 3.25) * mm, "end": v(-24.25, 9.75) * mm});
            skLineSegment(sketch, "E135.0.0", {"start": v(-24.25, -3.25) * mm, "end": v(-22, -3.25) * mm});
            skLineSegment(sketch, "E135.0.1", {"start": v(-22, -3.25) * mm, "end": v(-22, -9.75) * mm});
            skLineSegment(sketch, "E135.0.2", {"start": v(-22, -9.75) * mm, "end": v(-24.25, -9.75) * mm});
            skLineSegment(sketch, "E135.0.3", {"start": v(-24.25, -9.75) * mm, "end": v(-24.25, -3.25) * mm});
            skLineSegment(sketch, "E136", {"start": v(-84, 16.25) * mm, "end": v(-22, 16.25) * mm});
            skLineSegment(sketch, "E137", {"start": v(-84, -16.25) * mm, "end": v(-22, -16.25) * mm});
            skLineSegment(sketch, "E138", {"start": v(-10.25, -10.25) * mm, "end": v(-8.66, -11.84) * mm});
            skLineSegment(sketch, "E139", {"start": v(-8.66, -11.84) * mm, "end": v(-4.07, -7.25) * mm});
            skLineSegment(sketch, "E140", {"start": v(-4.07, -7.25) * mm, "end": v(-5.66, -5.66) * mm});
            skLineSegment(sketch, "E141", {"start": v(-5.66, -5.66) * mm, "end": v(0, 0) * mm});
            skLineSegment(sketch, "E142.1.0", {"start": v(-5.66, 5.66) * mm, "end": v(0, 0) * mm});
            skLineSegment(sketch, "E142.1.1", {"start": v(-7.25, 4.07) * mm, "end": v(-5.66, 5.66) * mm});
            skLineSegment(sketch, "E142.1.2", {"start": v(-10.25, 10.25) * mm, "end": v(-11.84, 8.66) * mm});
            skLineSegment(sketch, "E142.1.3", {"start": v(-11.84, 8.66) * mm, "end": v(-7.25, 4.07) * mm});
            skPoint(sketch, "E142.center", {"position": v(0, 0) * mm});
            skLineSegment(sketch, "E142.anchor1", {"start": v(0, 0) * mm, "end": v(-10.25, -10.25) * mm, "construction": true});
            skLineSegment(sketch, "E142.anchor2", {"start": v(0, 0) * mm, "end": v(-10.25, 10.25) * mm, "construction": true});
            skLineSegment(sketch, "E143", {"start": v(0, 0) * mm, "end": v(-22, 0) * mm, "construction": true});
            skLineSegment(sketch, "E144", {"start": v(-10.25, -10.25) * mm, "end": v(-12.37, -12.37) * mm});
            skLineSegment(sketch, "E145", {"start": v(-12.37, -12.37) * mm, "end": v(-22, -16.25) * mm});
            skLineSegment(sketch, "E146.MirrorCS", {"start": v(-12.37, 12.37) * mm, "end": v(-22, 16.25) * mm});
            skLineSegment(sketch, "E147.MirrorCS", {"start": v(-10.25, 10.25) * mm, "end": v(-12.37, 12.37) * mm});
            skLineSegment(sketch, "E148.0", {"start": v(-86.25, -9.75) * mm, "end": v(-84, -9.75) * mm});
            skLineSegment(sketch, "E149.0", {"start": v(-86.25, -3.25) * mm, "end": v(-84, -3.25) * mm});
            skLineSegment(sketch, "E150.0", {"start": v(-86.25, 3.25) * mm, "end": v(-84, 3.25) * mm});
            skLineSegment(sketch, "E151.0", {"start": v(-86.25, 9.75) * mm, "end": v(-84, 9.75) * mm});
            skLineSegment(sketch, "E152.0", {"start": v(-86.25, 9.75) * mm, "end": v(-86.25, 3.25) * mm});
            skLineSegment(sketch, "E153.0", {"start": v(-86.25, -3.25) * mm, "end": v(-86.25, -9.75) * mm});
            skLineSegment(sketch, "E154.0", {"start": v(-84, 3.25) * mm, "end": v(-84, -3.25) * mm});
            skLineSegment(sketch, "E155", {"start": v(-84, -16.25) * mm, "end": v(-84, -9.75) * mm});
            skLineSegment(sketch, "E156", {"start": v(-84, 9.75) * mm, "end": v(-84, 16.25) * mm});
            skLineSegment(sketch, "E157.bottom", {"start": v(-78, 1.12) * mm, "end": v(-74, 1.12) * mm});
            skLineSegment(sketch, "E157.top", {"start": v(-78, -1.12) * mm, "end": v(-74, -1.13) * mm});
            skLineSegment(sketch, "E157.left", {"start": v(-78, 1.13) * mm, "end": v(-78, -1.13) * mm});
            skLineSegment(sketch, "E157.right", {"start": v(-74, 1.13) * mm, "end": v(-74, -1.13) * mm});
            skLineSegment(sketch, "E158.bottom", {"start": v(-70, 1.12) * mm, "end": v(-66, 1.12) * mm});
            skLineSegment(sketch, "E158.top", {"start": v(-70, -1.13) * mm, "end": v(-66, -1.13) * mm});
            skLineSegment(sketch, "E158.left", {"start": v(-70, 1.13) * mm, "end": v(-70, -1.13) * mm});
            skLineSegment(sketch, "E158.right", {"start": v(-66, 1.12) * mm, "end": v(-66, -1.12) * mm});
            skLineSegment(sketch, "E159", {"start": v(-74, -1.13) * mm, "end": v(-70, -1.13) * mm, "construction": true});
            skLineSegment(sketch, "E160", {"start": v(-78, 0) * mm, "end": v(-82, 0) * mm, "construction": true});
            skPoint(sketch, "E160.endSnap0", {"position": v(-78, 0) * mm});
            skSolve(sketch);
        }
        {
            var Q0;
            Q0=makeQuery(id+"F21.imprint","IMPRINT",FACE,{"disambiguationData":[TD([[makeQuery(id+"F21.imprint","IMPRINT",EDGE,{"derivedFrom":sQuery(id+"F21.wireOp",EDGE,"E134.0.0")}),1.0]])]});
            extrude(context, id + "F22", {"entities" : qUnion([Q0]), "depth" : (getVariable(context, 'ep')) * mm});
        }
        {
            var Q0;
            Q0=makeQuery(id+"F22.opExtrude","SWEPT_FACE",FACE,{"disambiguationData":[OSD([sQuery(id+"F21.wireOp",EDGE,"E157.bottom")])]});
            var sketch = newSketch(context, id + "F23", { "sketchPlane" : qUnion([Q0])});
            skLineSegment(sketch, "E161.0", {"start": v(-78, 2.25) * mm, "end": v(-78, 0) * mm});
            skLineSegment(sketch, "E162.0", {"start": v(-78, 0) * mm, "end": v(-74, 0) * mm});
            skLineSegment(sketch, "E163.0", {"start": v(-74, 2.25) * mm, "end": v(-74, 0) * mm});
            skLineSegment(sketch, "E164.0", {"start": v(-66, 2.25) * mm, "end": v(-66, 0) * mm});
            skLineSegment(sketch, "E165.0", {"start": v(-70, 0) * mm, "end": v(-66, 0) * mm});
            skLineSegment(sketch, "E166.0", {"start": v(-70, 2.25) * mm, "end": v(-70, 0) * mm});
            skLineSegment(sketch, "E167", {"start": v(-78, 2.25) * mm, "end": v(-82, 2.25) * mm});
            skLineSegment(sketch, "E168", {"start": v(-82, 2.25) * mm, "end": v(-82, 6.25) * mm});
            skLineSegment(sketch, "E169", {"start": v(-82, 6.25) * mm, "end": v(-62, 6.25) * mm});
            skLineSegment(sketch, "E170", {"start": v(-62, 6.25) * mm, "end": v(-62, 2.25) * mm});
            skLineSegment(sketch, "E171", {"start": v(-62, 2.25) * mm, "end": v(-66, 2.25) * mm});
            skLineSegment(sketch, "E172", {"start": v(-70, 2.25) * mm, "end": v(-74, 2.25) * mm});
            skSolve(sketch);
        }
        {
            var Q0;
            Q0=qSketchRegion(id+"F23",true);
            var Q1;
            Q1=makeQuery(id+"F22.opExtrude","SWEPT_FACE",FACE,{"disambiguationData":[OSD([sQuery(id+"F21.wireOp",EDGE,"E157.top")])]});
            extrude(context, id + "F24", {"entities" : qUnion([Q0]), "endBound" : BoundingType.UP_TO_SURFACE, "endBoundEntityFace" : qUnion([Q1]), "depth" : 25 * mm});
        }
        {
            var Q0;
            Q0=makeQuery(id+"F6.opExtrude","SWEPT_BODY",BODY,{"disambiguationData":[OSD([sQuery(id+"F5.wireOp",EDGE,"E26.left"),sQuery(id+"F5.wireOp",EDGE,"E30"),sQuery(id+"F5.wireOp",EDGE,"E31"),sQuery(id+"F5.wireOp",EDGE,"E32")])]});
            var Q1;
            Q1=makeQuery(id+"F22.opExtrude","SWEPT_BODY",BODY,{"disambiguationData":[OSD([sQuery(id+"F21.wireOp",EDGE,"E134.0.0"),sQuery(id+"F21.wireOp",EDGE,"E134.0.1"),sQuery(id+"F21.wireOp",EDGE,"E134.0.2"),sQuery(id+"F21.wireOp",EDGE,"E134.0.3"),sQuery(id+"F21.wireOp",EDGE,"E135.0.0"),sQuery(id+"F21.wireOp",EDGE,"E135.0.1"),sQuery(id+"F21.wireOp",EDGE,"E135.0.2"),sQuery(id+"F21.wireOp",EDGE,"E135.0.3"),sQuery(id+"F21.wireOp",EDGE,"E136"),sQuery(id+"F21.wireOp",EDGE,"E137"),sQuery(id+"F21.wireOp",EDGE,"E138"),sQuery(id+"F21.wireOp",EDGE,"E139"),sQuery(id+"F21.wireOp",EDGE,"E140"),sQuery(id+"F21.wireOp",EDGE,"E141"),sQuery(id+"F21.wireOp",EDGE,"E142.1.0"),sQuery(id+"F21.wireOp",EDGE,"E142.1.1"),sQuery(id+"F21.wireOp",EDGE,"E142.1.2"),sQuery(id+"F21.wireOp",EDGE,"E142.1.3"),sQuery(id+"F21.wireOp",EDGE,"E144"),sQuery(id+"F21.wireOp",EDGE,"E145"),sQuery(id+"F21.wireOp",EDGE,"E146.MirrorCS"),sQuery(id+"F21.wireOp",EDGE,"E147.MirrorCS"),sQuery(id+"F21.wireOp",EDGE,"tspblnoj-Dp5W-AzlG-uek7-DDTLVZN02IB6.right")])]});
            var Q2;
            Q2=makeQuery(id+"F12.opExtrude","SWEPT_BODY",BODY,{"disambiguationData":[OSD([sQuery(id+"F11.wireOp",EDGE,"E50.bottom"),sQuery(id+"F11.wireOp",EDGE,"E50.top"),sQuery(id+"F11.wireOp",EDGE,"E50.left"),sQuery(id+"F11.wireOp",EDGE,"E50.right")])]});
            var Q3;
            Q3=makeQuery(id+"F14.opExtrude","SWEPT_BODY",BODY,{"disambiguationData":[OSD([sQuery(id+"F13.wireOp",EDGE,"E51.0"),sQuery(id+"F13.wireOp",EDGE,"E51.1"),sQuery(id+"F13.wireOp",EDGE,"E51.2"),sQuery(id+"F13.wireOp",EDGE,"E51.3"),sQuery(id+"F13.wireOp",EDGE,"E52.0"),sQuery(id+"F13.wireOp",EDGE,"E52.1"),sQuery(id+"F13.wireOp",EDGE,"E52.2"),sQuery(id+"F13.wireOp",EDGE,"E52.3"),sQuery(id+"F13.wireOp",EDGE,"wZcKvyZ9-swz3-P67m-EJlE-V8fpUGM8ZBwq"),sQuery(id+"F13.wireOp",EDGE,"E53"),sQuery(id+"F13.wireOp",EDGE,"E54.top"),sQuery(id+"F13.wireOp",EDGE,"E54.right"),sQuery(id+"F13.wireOp",EDGE,"E55.bottom"),sQuery(id+"F13.wireOp",EDGE,"E55.top"),sQuery(id+"F13.wireOp",EDGE,"E55.right"),sQuery(id+"F13.wireOp",EDGE,"E56.bottom"),sQuery(id+"F13.wireOp",EDGE,"E56.top"),sQuery(id+"F13.wireOp",EDGE,"E56.right"),sQuery(id+"F13.wireOp",EDGE,"E57.trimOffspring"),sQuery(id+"F13.wireOp",EDGE,"E58.bottom"),sQuery(id+"F13.wireOp",EDGE,"E58.top"),sQuery(id+"F13.wireOp",EDGE,"E58.right"),sQuery(id+"F13.wireOp",EDGE,"E59.bottom"),sQuery(id+"F13.wireOp",EDGE,"E59.top"),sQuery(id+"F13.wireOp",EDGE,"E59.right"),sQuery(id+"F13.wireOp",EDGE,"E60.trimOffspring"),sQuery(id+"F13.wireOp",EDGE,"E61.trimOffspring")])]});
            var Q4;
            Q4=makeQuery(id+"F16.opExtrude","SWEPT_BODY",BODY,{"disambiguationData":[OSD([sQuery(id+"F15.wireOp",EDGE,"E83.0"),sQuery(id+"F15.wireOp",EDGE,"E84.0"),sQuery(id+"F15.wireOp",EDGE,"E85.0"),sQuery(id+"F15.wireOp",EDGE,"E86.0"),sQuery(id+"F15.wireOp",EDGE,"E87.0"),sQuery(id+"F15.wireOp",EDGE,"E88.0"),sQuery(id+"F15.wireOp",EDGE,"E89"),sQuery(id+"F15.wireOp",EDGE,"E90"),sQuery(id+"F15.wireOp",EDGE,"E91"),sQuery(id+"F15.wireOp",EDGE,"E93.MirrorCS"),sQuery(id+"F15.wireOp",EDGE,"E94.MirrorCS"),sQuery(id+"F15.wireOp",EDGE,"E95.MirrorCS"),sQuery(id+"F15.wireOp",EDGE,"E96.MirrorCS"),sQuery(id+"F15.wireOp",EDGE,"E97.MirrorCS"),sQuery(id+"F15.wireOp",EDGE,"E98.MirrorCS"),sQuery(id+"F15.wireOp",EDGE,"E99.MirrorCS"),sQuery(id+"F15.wireOp",EDGE,"E100.MirrorCS"),sQuery(id+"F15.wireOp",EDGE,"E101.MirrorCS"),sQuery(id+"F15.wireOp",EDGE,"E102"),sQuery(id+"F15.wireOp",EDGE,"E103")])]});
            var Q5;
            Q5=makeQuery(id+"F18.opExtrude","SWEPT_BODY",BODY,{"disambiguationData":[OSD([sQuery(id+"F17.wireOp",EDGE,"E110.0"),sQuery(id+"F17.wireOp",EDGE,"E111.0"),sQuery(id+"F17.wireOp",EDGE,"E112.0"),sQuery(id+"F17.wireOp",EDGE,"E113"),sQuery(id+"F17.wireOp",EDGE,"E114"),sQuery(id+"F17.wireOp",EDGE,"E115"),sQuery(id+"F17.wireOp",EDGE,"E116"),sQuery(id+"F17.wireOp",EDGE,"E117"),sQuery(id+"F17.wireOp",EDGE,"E118"),sQuery(id+"F17.wireOp",EDGE,"E119"),sQuery(id+"F17.wireOp",EDGE,"E120"),sQuery(id+"F17.wireOp",EDGE,"E121")])]});
            var Q6;
            Q6=makeQuery(id+"F20.opExtrude","SWEPT_BODY",BODY,{"disambiguationData":[OSD([sQuery(id+"F19.wireOp",EDGE,"E122.0"),sQuery(id+"F19.wireOp",EDGE,"E123.0"),sQuery(id+"F19.wireOp",EDGE,"E124.0"),sQuery(id+"F19.wireOp",EDGE,"E125.0"),sQuery(id+"F19.wireOp",EDGE,"E126.0"),sQuery(id+"F19.wireOp",EDGE,"E127.0"),sQuery(id+"F19.wireOp",EDGE,"E128.0"),sQuery(id+"F19.wireOp",EDGE,"E129.0"),sQuery(id+"F19.wireOp",EDGE,"E130"),sQuery(id+"F19.wireOp",EDGE,"E131"),sQuery(id+"F19.wireOp",EDGE,"E132"),sQuery(id+"F19.wireOp",EDGE,"E133")])]});
            var Q7;
            Q7=makeQuery(id+"F24.opExtrude","SWEPT_BODY",BODY,{"disambiguationData":[OSD([sQuery(id+"F23.wireOp",EDGE,"E161.0"),sQuery(id+"F23.wireOp",EDGE,"E162.0"),sQuery(id+"F23.wireOp",EDGE,"E163.0"),sQuery(id+"F23.wireOp",EDGE,"E164.0"),sQuery(id+"F23.wireOp",EDGE,"E165.0"),sQuery(id+"F23.wireOp",EDGE,"E166.0"),sQuery(id+"F23.wireOp",EDGE,"E167"),sQuery(id+"F23.wireOp",EDGE,"E168"),sQuery(id+"F23.wireOp",EDGE,"E169"),sQuery(id+"F23.wireOp",EDGE,"E170"),sQuery(id+"F23.wireOp",EDGE,"E171"),sQuery(id+"F23.wireOp",EDGE,"E172")])]});
            var Q8;
            Q8=sQuery(id+"F1.wireOp",EDGE,"E17");
            circularPattern(context, id + "F25", {"entities" : qUnion([Q0, Q1, Q2, Q3, Q4, Q5, Q6, Q7]), "axis" : qUnion([Q8]), "angle" : 360 * degree, "instanceCount" : 4, "equalSpace" : true});
        }
    });
